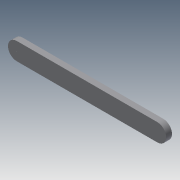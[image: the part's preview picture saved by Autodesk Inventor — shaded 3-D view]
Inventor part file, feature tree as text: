
AUTODESK INVENTOR PART (.ipt)
format: ipt  version: 2013 (Build 170138000, 138)  size: 74,240 bytes
history: native  units: mm
features: extrude x1, sketch x1
ambient origin geometry x8: Origin, YZ Plane, XZ Plane, XY Plane, X Axis, Y Axis, Z Axis, Center Point
bodies: Solid1 (feature_tree)
feature tree (2):
  extrude  "Extrusion1"  Depth=6.0mm
  sketch  "Sketch1"  dims[d0=48.0mm d1=6.0mm d3=0.1mm d4=0.1mm d5=2.0mm d6=0.0mm]
